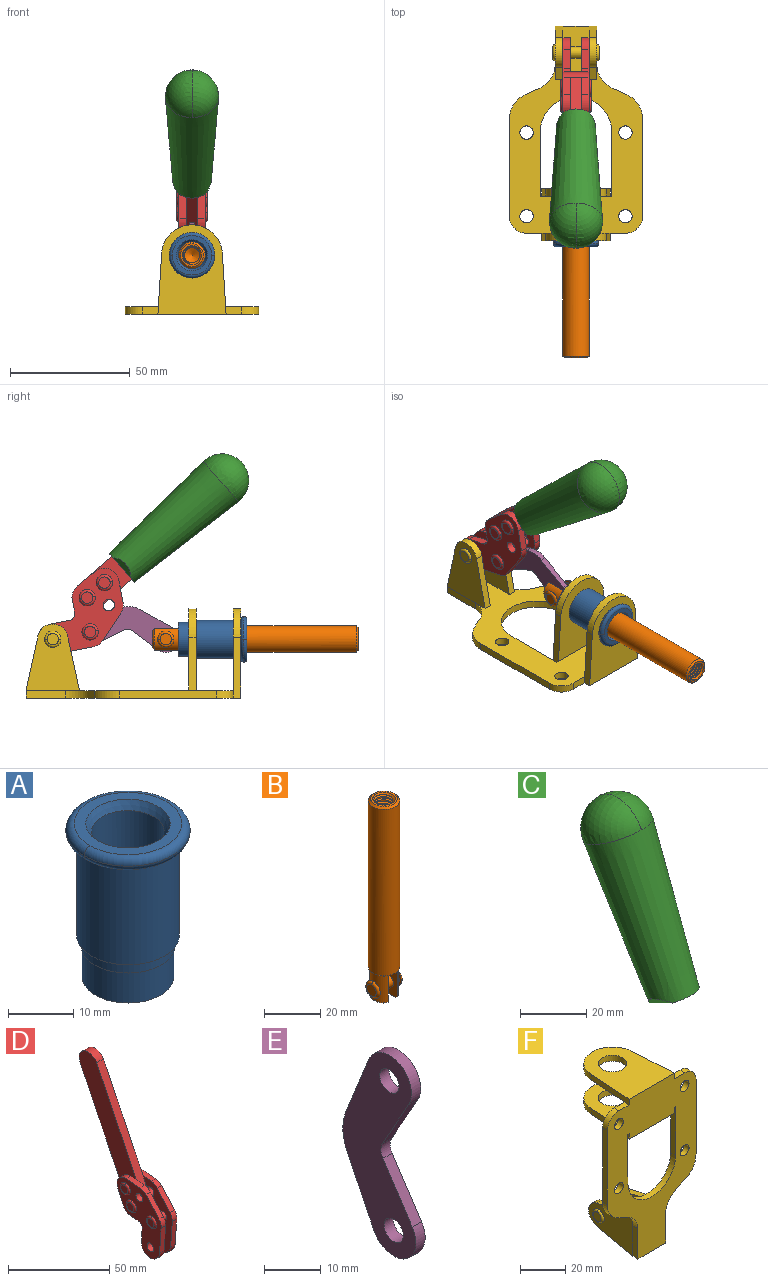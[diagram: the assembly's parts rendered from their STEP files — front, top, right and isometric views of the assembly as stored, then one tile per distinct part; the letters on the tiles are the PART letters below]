
ASSEMBLY  parts=6 mates=6
PART A: 15 faces, bbox 20.6x20.6x28.7 mm
  f0: torus R=8.26mm, axis (0,0,1), area 56.8mm2, adj f1,f10,f12
  f1: torus R=8.26mm, axis (0,0,1), area 56.8mm2, adj f0,f6,f13
  f2: cylinder r=5.59mm len=25.91mm, axis (0,0,1), area 909.6mm2, adj f3,f4
  f3: cone r=6.86mm half-angle=45deg, axis (0,0,-1), area 70.2mm2, adj f2,f14
  f4: cone r=6.47mm half-angle=30deg, axis (0,0,1), area 66.7mm2, adj f2,f13
  f5: cylinder r=7.04mm len=14.07mm, axis (0,0,1), area 252.6mm2, adj f11,f14
  f6: torus R=8.26mm, axis (0,0,1), area 56.8mm2, adj f1,f12,f13
  f7: cylinder r=7.16mm len=14.33mm, axis (0,0,1), area 91.5mm2, adj f9,f11
  f8: cylinder r=7.86mm len=18.42mm, axis (0,0,1), area 909.6mm2, adj f9,f10
  f9: plane 15.72x15.72mm, normal (0,0,-1), area 33mm2, adj f7,f8
  f10: plane 16.51x16.51mm, normal (0,0,-1), area 19.9mm2, adj f0,f8,f12
  f11: plane 14.33x14.33mm, normal (0,0,-1), area 5.7mm2, adj f5,f7
  f12: torus R=8.26mm, axis (0,0,1), area 56.8mm2, adj f0,f6,f10
  f13: plane 16.51x16.51mm, normal (0,0,1), area 82.7mm2, adj f1,f4,f6
  f14: plane 14.07x14.07mm, normal (0,0,-1), area 7.8mm2, adj f3,f5
PART B: 48 faces, bbox 12.6x11.1x86.1 mm
  f0: torus R=2.41mm, axis (-1,0,0), area 15mm2, adj f30,f32,f34
  f1: torus R=2.41mm, axis (-1,0,0), area 15mm2, adj f29,f31,f33
  f2: cylinder r=5.54mm len=72.39mm, axis (0,0,1), area 2518.5mm2, adj f3,f4,f42,f43
  f3: cone r=5.54mm half-angle=45deg, axis (0,0,1), area 7.6mm2, adj f2,f5,f41
  f4: cone r=5.54mm half-angle=45deg, axis (0,0,-1), area 34.9mm2, adj f2,f39
  f5: cylinder r=5.08mm len=11.48mm, axis (0,0,1), area 108.3mm2, adj f3,f7,f8,f41
  f6: cylinder r=2.41mm len=4.83mm, axis (-1,0,0), area 71.2mm2, adj f40,f41
  f7: cylinder r=2.41mm len=4.83mm, axis (-1,0,0), area 7.6mm2, adj f5,f34
  f8: cone r=5.08mm half-angle=45deg, axis (0,0,1), area 10.6mm2, adj f5,f37,f41
  f9: cone r=3.98mm half-angle=45deg, axis (0,0,1), area 17.6mm2, adj f27,f39,f45,f46,f47
  f10: cylinder r=2.41mm len=4.83mm, axis (-1,0,0), area 7.6mm2, adj f33,f38
  f11: cylinder r=3.2mm len=6.4mm, axis (0,0,1), area 78.4mm2, adj f12,f28,f44,f45,f47
  f12: cylinder r=3.2mm len=6.4mm, axis (0,0,1), area 10.5mm2, adj f11,f13,f45,f47
  f13: cylinder r=3.2mm len=6.4mm, axis (0,0,1), area 10.5mm2, adj f12,f14,f45,f47
  f14: cylinder r=3.2mm len=6.4mm, axis (0,0,1), area 10.5mm2, adj f13,f15,f45,f47
  f15: cylinder r=3.2mm len=6.4mm, axis (0,0,1), area 10.5mm2, adj f14,f16,f45,f47
  f16: cylinder r=3.2mm len=6.4mm, axis (0,0,1), area 10.5mm2, adj f15,f17,f45,f47
  f17: cylinder r=3.2mm len=6.4mm, axis (0,0,1), area 10.5mm2, adj f16,f18,f45,f47
  f18: cylinder r=3.2mm len=6.4mm, axis (0,0,1), area 10.5mm2, adj f17,f19,f45,f47
  f19: cylinder r=3.2mm len=6.4mm, axis (0,0,1), area 10.5mm2, adj f18,f20,f45,f47
  f20: cylinder r=3.2mm len=6.4mm, axis (0,0,1), area 10.5mm2, adj f19,f21,f45,f47
  f21: cylinder r=3.2mm len=6.4mm, axis (0,0,1), area 10.5mm2, adj f20,f22,f45,f47
  f22: cylinder r=3.2mm len=6.4mm, axis (0,0,1), area 10.5mm2, adj f21,f23,f45,f47
  f23: cylinder r=3.2mm len=6.4mm, axis (0,0,1), area 10.5mm2, adj f22,f24,f45,f47
  f24: cylinder r=3.2mm len=6.4mm, axis (0,0,1), area 10.5mm2, adj f23,f25,f45,f47
  f25: cylinder r=3.2mm len=6.4mm, axis (0,0,1), area 10.5mm2, adj f24,f26,f45,f47
  f26: cylinder r=3.2mm len=6.4mm, axis (0,0,1), area 10.5mm2, adj f25,f27,f45,f47
  f27: cylinder r=3.2mm len=6.4mm, axis (0,0,1), area 7.4mm2, adj f9,f26,f45,f47
  f28: cone r=3.2mm half-angle=60deg, axis (0,0,1), area 37.2mm2, adj f11
  f29: plane 4.83x4.83mm, normal (-1,0,0), area 18.3mm2, adj f1,f31
  f30: plane 4.83x4.83mm, normal (1,0,0), area 18.3mm2, adj f0,f32
  f31: torus R=2.41mm, axis (-1,0,0), area 15mm2, adj f1,f29,f33
  f32: torus R=2.41mm, axis (-1,0,0), area 15mm2, adj f0,f30,f34
  f33: plane 6.83x6.83mm, normal (1,0,0), area 18.3mm2, adj f1,f10,f31
  f34: plane 6.83x6.83mm, normal (-1,0,0), area 18.3mm2, adj f0,f7,f32
  f35: cone r=5.08mm half-angle=45deg, axis (0,0,1), area 10.6mm2, adj f36,f38,f40
  f36: plane 7.25x1.97mm, normal (0,0,-1), area 10mm2, adj f35,f40
  f37: plane 7.25x1.97mm, normal (0,0,-1), area 10mm2, adj f8,f41
  f38: cylinder r=5.08mm len=11.48mm, axis (0,0,1), area 108.3mm2, adj f10,f35,f40,f42
  f39: plane 9.55x9.55mm, normal (0,0,1), area 22mm2, adj f4,f9
  f40: plane 12.76x10.09mm, normal (1,0,0), area 95.7mm2, adj f6,f35,f36,f38,f42,f43
  f41: plane 12.76x10.09mm, normal (-1,0,0), area 95.7mm2, adj f3,f5,f6,f8,f37,f43
  f42: cone r=5.54mm half-angle=45deg, axis (0,0,1), area 7.6mm2, adj f2,f38,f40
  f43: plane 11.07x4.7mm, normal (0,0,-1), area 50.4mm2, adj f2,f40,f41
  f44: plane 0.89x0.62mm, normal (-1,0,0), area 0.3mm2, adj f11,f45,f46,f47
  f45: bspline ~24.8x7.63mm, area 266.6mm2, adj f9,f11,f12,f13,f14,f15,f16,f17
  f46: bspline ~24.87x7.63mm, area 73.6mm2, adj f9,f44,f45,f47
  f47: bspline ~24.98x7.63mm, area 272.5mm2, adj f9,f11,f12,f13,f14,f15,f16,f17
PART C: 11 faces, bbox 22.3x42.6x64.5 mm
  f0: sphere r=11.13mm, area 411.4mm2, adj f1,f8
  f1: cone r=11.11mm half-angle=3.3deg, axis (0,0.44,0.9), area 3251.8mm2, adj f0,f7,f8,f9,f10
  f2: cylinder r=6.16mm len=11.7mm, axis (1,0,0), area 89.5mm2, adj f3,f4,f5,f6
  f3: plane 60.23x36.75mm, normal (-1,0,0), area 763.6mm2, adj f2,f4,f6,f10
  f4: plane 51.37x25.05mm, normal (0,0.9,-0.44), area 264.2mm2, adj f2,f3,f5,f10
  f5: plane 60.23x36.75mm, normal (1,0,0), area 763.6mm2, adj f2,f4,f6,f10
  f6: plane 51.37x25.05mm, normal (0,-0.9,0.44), area 264.2mm2, adj f2,f3,f5,f10
  f7: plane 9.95x5.95mm, normal (0.71,-0.31,-0.64), area 25.8mm2, adj f1,f10
  f8: sphere r=11.13mm, area 411.4mm2, adj f0,f1
  f9: plane 9.95x5.95mm, normal (-0.71,-0.31,-0.64), area 25.8mm2, adj f1,f10
  f10: plane 14.27x11.38mm, normal (0,-0.44,-0.9), area 106.7mm2, adj f1,f3,f4,f5,f6,f7,f9
PART D: 59 faces, bbox 12.9x60.2x99.6 mm
  f0: torus R=2.39mm, axis (-1,0,0), area 14.9mm2, adj f20,f43,f51
  f1: torus R=2.39mm, axis (-1,0,0), area 14.9mm2, adj f19,f42,f51
  f2: torus R=2.39mm, axis (-1,0,0), area 14.9mm2, adj f18,f35,f51
  f3: torus R=2.39mm, axis (-1,0,0), area 14.9mm2, adj f14,f17,f23
  f4: torus R=2.39mm, axis (-1,0,0), area 14.9mm2, adj f13,f16,f23
  f5: torus R=2.39mm, axis (-1,0,0), area 14.9mm2, adj f12,f15,f23
  f6: cylinder r=2.39mm len=4.78mm, axis (1,0,0), area 46.5mm2, adj f48,f50,f51
  f7: cylinder r=2.39mm len=4.78mm, axis (1,0,0), area 46.5mm2, adj f50,f51
  f8: cylinder r=6.35mm len=12.68mm, axis (1,0,0), area 61.8mm2, adj f38,f39,f50,f51
  f9: cylinder r=2.39mm len=4.78mm, axis (-1,0,0), area 70.5mm2, adj f46,f50
  f10: cylinder r=2.39mm len=4.78mm, axis (-1,0,0), area 46.5mm2, adj f23,f45,f46
  f11: cylinder r=2.39mm len=4.78mm, axis (-1,0,0), area 46.5mm2, adj f23,f46
  f12: plane 4.78x4.78mm, normal (1,0,0), area 17.9mm2, adj f5,f15
  f13: plane 4.78x4.78mm, normal (1,0,0), area 17.9mm2, adj f4,f16
  f14: plane 4.78x4.78mm, normal (1,0,0), area 17.9mm2, adj f3,f17
  f15: torus R=2.39mm, axis (-1,0,0), area 14.9mm2, adj f5,f12,f23
  f16: torus R=2.39mm, axis (-1,0,0), area 14.9mm2, adj f4,f13,f23
  f17: torus R=2.39mm, axis (-1,0,0), area 14.9mm2, adj f3,f14,f23
  f18: plane 4.78x4.78mm, normal (-1,0,0), area 17.9mm2, adj f2,f35
  f19: plane 4.78x4.78mm, normal (-1,0,0), area 17.9mm2, adj f1,f42
  f20: plane 4.78x4.78mm, normal (-1,0,0), area 17.9mm2, adj f0,f43
  f21: plane 2.26x0.2mm, normal (1,0,0), area 0.2mm2, adj f31,f44
  f22: plane 2.26x0.2mm, normal (-1,0,0), area 0.2mm2, adj f41,f44
  f23: plane 39.37x30.77mm, normal (1,0,0), area 565.5mm2, adj f3,f4,f5,f10,f11,f15,f16,f17
  f24: cylinder r=6.1mm len=4.15mm, axis (-1,0,0), area 14.7mm2, adj f23,f25,f32,f46
  f25: plane 10.25x9.01mm, normal (0,-0.75,0.66), area 42.3mm2, adj f23,f24,f26,f46
  f26: cylinder r=6.35mm len=4.64mm, axis (-1,0,0), area 15.6mm2, adj f23,f25,f27,f46
  f27: plane 15.84x3.1mm, normal (0,-1,-0.07), area 49.2mm2, adj f23,f26,f28,f46
  f28: cylinder r=6.35mm len=12.68mm, axis (-1,0,0), area 61.8mm2, adj f23,f27,f29,f46
  f29: plane 8.11x3.1mm, normal (0,1,0.07), area 25.2mm2, adj f23,f28,f30,f46
  f30: cylinder r=3.05mm len=3.25mm, axis (-1,0,0), area 14.8mm2, adj f23,f29,f31,f46
  f31: plane 5.99x3.1mm, normal (0,0.07,-1), area 18.6mm2, adj f21,f23,f30,f44,f46
  f32: plane 9.5x3.1mm, normal (0,-0.07,1), area 29.5mm2, adj f23,f24,f33,f46,f47
  f33: cylinder r=6.1mm len=8.63mm, axis (-1,0,0), area 39.1mm2, adj f23,f32,f34,f47
  f34: plane 8.65x3.96mm, normal (0,0.91,-0.42), area 29.5mm2, adj f23,f33,f44,f47
  f35: torus R=2.39mm, axis (-1,0,0), area 14.9mm2, adj f2,f18,f51
  f36: plane 10.25x9.01mm, normal (0,-0.75,0.66), area 42.3mm2, adj f37,f49,f50,f51
  f37: cylinder r=6.35mm len=4.64mm, axis (1,0,0), area 15.6mm2, adj f36,f38,f50,f51
  f38: plane 15.84x3.1mm, normal (0,-1,-0.07), area 49.2mm2, adj f8,f37,f50,f51
  f39: plane 8.11x3.1mm, normal (0,1,0.07), area 25.2mm2, adj f8,f40,f50,f51
  f40: cylinder r=3.05mm len=3.25mm, axis (1,0,0), area 14.8mm2, adj f39,f41,f50,f51
  f41: plane 5.99x3.1mm, normal (0,0.07,-1), area 18.6mm2, adj f22,f40,f44,f50,f51
  f42: torus R=2.39mm, axis (-1,0,0), area 14.9mm2, adj f1,f19,f51
  f43: torus R=2.39mm, axis (-1,0,0), area 14.9mm2, adj f0,f20,f51
  f44: cylinder r=6.35mm len=12.12mm, axis (-1,0,0), area 128.9mm2, adj f21,f22,f23,f31,f34,f41,f46,f47
  f45: plane 2.65x1.35mm, normal (1,0,0), area 1mm2, adj f10,f55
  f46: plane 39.08x20.42mm, normal (-1,0,0), area 412.5mm2, adj f9,f10,f11,f24,f25,f26,f27,f28
  f47: plane 77.62x39.82mm, normal (1,0,0), area 850mm2, adj f32,f33,f34,f44,f53,f54,f55
  f48: plane 2.65x1.35mm, normal (-1,0,0), area 1mm2, adj f6,f55
  f49: cylinder r=6.1mm len=4.15mm, axis (1,0,0), area 14.7mm2, adj f36,f50,f51,f56
  f50: plane 39.08x20.42mm, normal (1,0,0), area 412.5mm2, adj f6,f7,f8,f9,f36,f37,f38,f39
  f51: plane 39.37x30.77mm, normal (-1,0,0), area 565.5mm2, adj f0,f1,f2,f6,f7,f8,f35,f36
  f52: plane 8.65x3.96mm, normal (0,0.91,-0.42), area 29.5mm2, adj f44,f51,f57,f58
  f53: plane 68.49x33.4mm, normal (0,0.9,-0.44), area 358.1mm2, adj f44,f47,f54,f58
  f54: cylinder r=6.35mm len=12.06mm, axis (1,0,0), area 93.7mm2, adj f47,f53,f55,f58
  f55: plane 68.49x33.4mm, normal (0,-0.9,0.44), area 358.1mm2, adj f44,f45,f46,f47,f48,f50,f54,f58
  f56: plane 9.5x3.1mm, normal (0,-0.07,1), area 29.5mm2, adj f49,f50,f51,f57,f58
  f57: cylinder r=6.1mm len=8.63mm, axis (1,0,0), area 39.1mm2, adj f51,f52,f56,f58
  f58: plane 77.62x39.82mm, normal (-1,0,0), area 850mm2, adj f44,f52,f53,f54,f55,f56,f57
PART E: 12 faces, bbox 2.3x18.2x42.8 mm
  f0: cylinder r=2.4mm len=4.8mm, axis (1,0,0), area 34.9mm2, adj f4,f11
  f1: cylinder r=10.41mm len=8.47mm, axis (1,0,0), area 20.2mm2, adj f4,f9,f10,f11
  f2: cylinder r=3.05mm len=3.16mm, axis (1,0,0), area 7.7mm2, adj f4,f6,f7,f11
  f3: cylinder r=2.4mm len=4.8mm, axis (1,0,0), area 34.9mm2, adj f4,f11
  f4: plane 42.81x18.23mm, normal (-1,0,0), area 414.1mm2, adj f0,f1,f2,f3,f5,f6,f7,f8
  f5: cylinder r=5.54mm len=10.67mm, axis (1,0,0), area 41.8mm2, adj f4,f6,f10,f11
  f6: plane 11.66x6.53mm, normal (0,-0.87,-0.49), area 30.9mm2, adj f2,f4,f5,f11
  f7: plane 11.17x7.33mm, normal (0,-0.84,0.55), area 30.9mm2, adj f2,f4,f8,f11
  f8: cylinder r=5.54mm len=10.51mm, axis (1,0,0), area 41.8mm2, adj f4,f7,f9,f11
  f9: plane 13.67x6.67mm, normal (0,0.9,-0.44), area 35.1mm2, adj f1,f4,f8,f11
  f10: plane 14.1x5.7mm, normal (0,0.93,0.37), area 35.1mm2, adj f1,f4,f5,f11
  f11: plane 42.81x18.23mm, normal (1,0,0), area 414.1mm2, adj f0,f1,f2,f3,f5,f6,f7,f8
PART F: 55 faces, bbox 55.7x37.4x89.8 mm
  f0: torus R=2.41mm, axis (-1,0,0), area 15mm2, adj f11,f15,f25
  f1: torus R=2.41mm, axis (-1,0,0), area 15mm2, adj f10,f12,f22
  f2: cylinder r=2.78mm len=5.56mm, axis (0,-1,0), area 54.2mm2, adj f30,f54
  f3: cylinder r=14.99mm len=29.97mm, axis (0,-1,0), area 145.9mm2, adj f30,f49,f53,f54
  f4: cylinder r=2.78mm len=5.56mm, axis (0,-1,0), area 54.2mm2, adj f30,f54
  f5: cylinder r=2.78mm len=5.56mm, axis (0,-1,0), area 54.2mm2, adj f30,f54
  f6: cylinder r=2.78mm len=5.56mm, axis (0,-1,0), area 54.2mm2, adj f30,f54
  f7: cylinder r=6.35mm len=12.7mm, axis (0,0,1), area 123.6mm2, adj f27,f51
  f8: cylinder r=6.35mm len=12.7mm, axis (0,0,-1), area 124.7mm2, adj f21,f35
  f9: cylinder r=2.41mm len=11.18mm, axis (-1,0,0), area 169.4mm2, adj f16,f19
  f10: plane 4.83x4.83mm, normal (1,0,0), area 18.3mm2, adj f1,f12
  f11: plane 4.83x4.83mm, normal (-1,0,0), area 18.3mm2, adj f0,f15
  f12: torus R=2.41mm, axis (-1,0,0), area 15mm2, adj f1,f10,f22
  f13: cylinder r=6.35mm len=12.41mm, axis (1,0,0), area 53.4mm2, adj f18,f19,f22,f23
  f14: cylinder r=6.35mm len=12.41mm, axis (-1,0,0), area 53.4mm2, adj f16,f17,f24,f25
  f15: torus R=2.41mm, axis (-1,0,0), area 15mm2, adj f0,f11,f25
  f16: plane 27.86x22.35mm, normal (1,0,0), area 425.4mm2, adj f9,f14,f17,f24,f30
  f17: plane 22.86x4.97mm, normal (0,0.21,0.98), area 72.5mm2, adj f14,f16,f25,f30
  f18: plane 22.86x4.97mm, normal (0,0.21,0.98), area 72.5mm2, adj f13,f19,f22,f30
  f19: plane 27.86x22.35mm, normal (-1,0,0), area 425.4mm2, adj f9,f13,f18,f23,f30
  f20: cylinder r=12.7mm len=25.35mm, axis (0,0,-1), area 119.8mm2, adj f21,f34,f35,f36
  f21: plane 34.21x28.07mm, normal (0,0,-1), area 702.4mm2, adj f8,f20,f30,f34,f36
  f22: plane 27.96x22.45mm, normal (1,0,0), area 407.2mm2, adj f1,f12,f13,f18,f23,f30,f42,f43
  f23: plane 22.86x4.97mm, normal (0,0.21,-0.98), area 72.5mm2, adj f13,f19,f22,f44
  f24: plane 22.86x4.97mm, normal (0,0.21,-0.98), area 72.5mm2, adj f14,f16,f25,f44
  f25: plane 27.86x22.35mm, normal (-1,0,0), area 407.1mm2, adj f0,f14,f15,f17,f24,f30,f45,f46
  f26: plane 3.1x0.95mm, normal (0,0,-1), area 2.7mm2, adj f30,f49,f50,f54
  f27: plane 34.21x28.07mm, normal (0,0,1), area 702.4mm2, adj f7,f28,f30,f50,f52
  f28: cylinder r=12.7mm len=25.35mm, axis (0,0,1), area 118.8mm2, adj f27,f50,f51,f52
  f29: plane 3.1x0.95mm, normal (0,0,-1), area 2.7mm2, adj f30,f52,f53,f54
  f30: plane 86.54x55.63mm, normal (0,1,0), area 2362.9mm2, adj f2,f3,f4,f5,f6,f16,f17,f18
  f31: plane 40.56x3.1mm, normal (-1,0,0), area 125.7mm2, adj f30,f32,f48,f54
  f32: cylinder r=7.11mm len=7.11mm, axis (0,-1,0), area 34.6mm2, adj f30,f31,f33,f54
  f33: plane 6.67x3.1mm, normal (0,0,1), area 20.4mm2, adj f30,f32,f34,f54
  f34: plane 25.39x3.13mm, normal (-1,0.06,0), area 79.5mm2, adj f20,f21,f33,f35,f54
  f35: plane 37.31x28.45mm, normal (0,0,1), area 789.9mm2, adj f8,f20,f34,f36,f54
  f36: plane 25.39x3.13mm, normal (1,0.06,0), area 79.5mm2, adj f20,f21,f35,f37,f54
  f37: plane 6.67x3.1mm, normal (0,0,1), area 20.4mm2, adj f30,f36,f38,f54
  f38: cylinder r=7.11mm len=7.11mm, axis (0,-1,0), area 34.6mm2, adj f30,f37,f39,f54
  f39: plane 40.56x3.1mm, normal (1,0,0), area 125.7mm2, adj f30,f38,f40,f54
  f40: cylinder r=11.18mm len=10.16mm, axis (0,-1,0), area 39.5mm2, adj f30,f39,f41,f54
  f41: plane 6.09x3.1mm, normal (0.42,0,-0.91), area 20.8mm2, adj f30,f40,f42,f54
  f42: cylinder r=11.18mm len=9.41mm, axis (0,-1,0), area 37.2mm2, adj f22,f30,f41,f43,f54
  f43: plane 16.5x3.1mm, normal (1,0,0), area 51.1mm2, adj f22,f42,f44,f54
  f44: plane 17.37x3.1mm, normal (0,0,-1), area 53.8mm2, adj f23,f24,f30,f43,f45,f54
  f45: plane 16.5x3.1mm, normal (-1,0,0), area 51.1mm2, adj f25,f44,f46,f54
  f46: cylinder r=11.18mm len=9.41mm, axis (0,-1,0), area 37.2mm2, adj f25,f30,f45,f47,f54
  f47: plane 6.09x3.1mm, normal (-0.42,0,-0.91), area 20.8mm2, adj f30,f46,f48,f54
  f48: cylinder r=11.18mm len=10.16mm, axis (0,-1,0), area 39.5mm2, adj f30,f31,f47,f54
  f49: plane 26.54x3.1mm, normal (-1,0,0), area 82.3mm2, adj f3,f26,f30,f54
  f50: plane 25.39x3.1mm, normal (1,0.06,0), area 78.8mm2, adj f26,f27,f28,f51,f54
  f51: plane 37.31x28.45mm, normal (0,0,-1), area 789.9mm2, adj f7,f28,f50,f52,f54
  f52: plane 25.39x3.1mm, normal (-1,0.06,0), area 78.8mm2, adj f27,f28,f29,f51,f54
  f53: plane 26.54x3.1mm, normal (1,0,0), area 82.3mm2, adj f3,f29,f30,f54
  f54: plane 89.66x55.63mm, normal (0,-1,0), area 2678.5mm2, adj f2,f3,f4,f5,f6,f26,f29,f31
PLACE A rot(axis=(1,0,0),90deg) t=(0,1.23,0)mm
PLACE B rot(axis=(1,0,0),90deg) t=(0,1.61,0)mm
PLACE C rot(axis=(1,0,0),75deg) t=(0,-4.04,9.14)mm
PLACE D rot(axis=(1,0,0),75deg) t=(0,-4.04,9.14)mm
PLACE E rot(axis=(1,0,0),97.5deg) t=(0,4.68,2.22)mm
PLACE F rot(axis=(1,0,0),90deg) t=(0,1.23,0)mm fixed
MATE fastened F.f7 <-> A.f0  axis (0,-1,0) through (0,-45.16,24.61)mm
MATE revolute E.f5 <-> B.f6  axis (1,0,0) through (0,-13.86,24.61)mm
MATE fastened C.f2 <-> D.f54  axis (1,0,0) through (0,-38.57,91.94)mm
MATE revolute E.f3 <-> D.f4  axis (1,0,0) through (0,17.74,27.64)mm
MATE slider F.f7 <-> B.f2  axis (0,-1,0) through (0,-45.16,24.61)mm
MATE revolute D.f7 <-> F.f0  axis (1,0,0) through (0,33.32,24.61)mm
